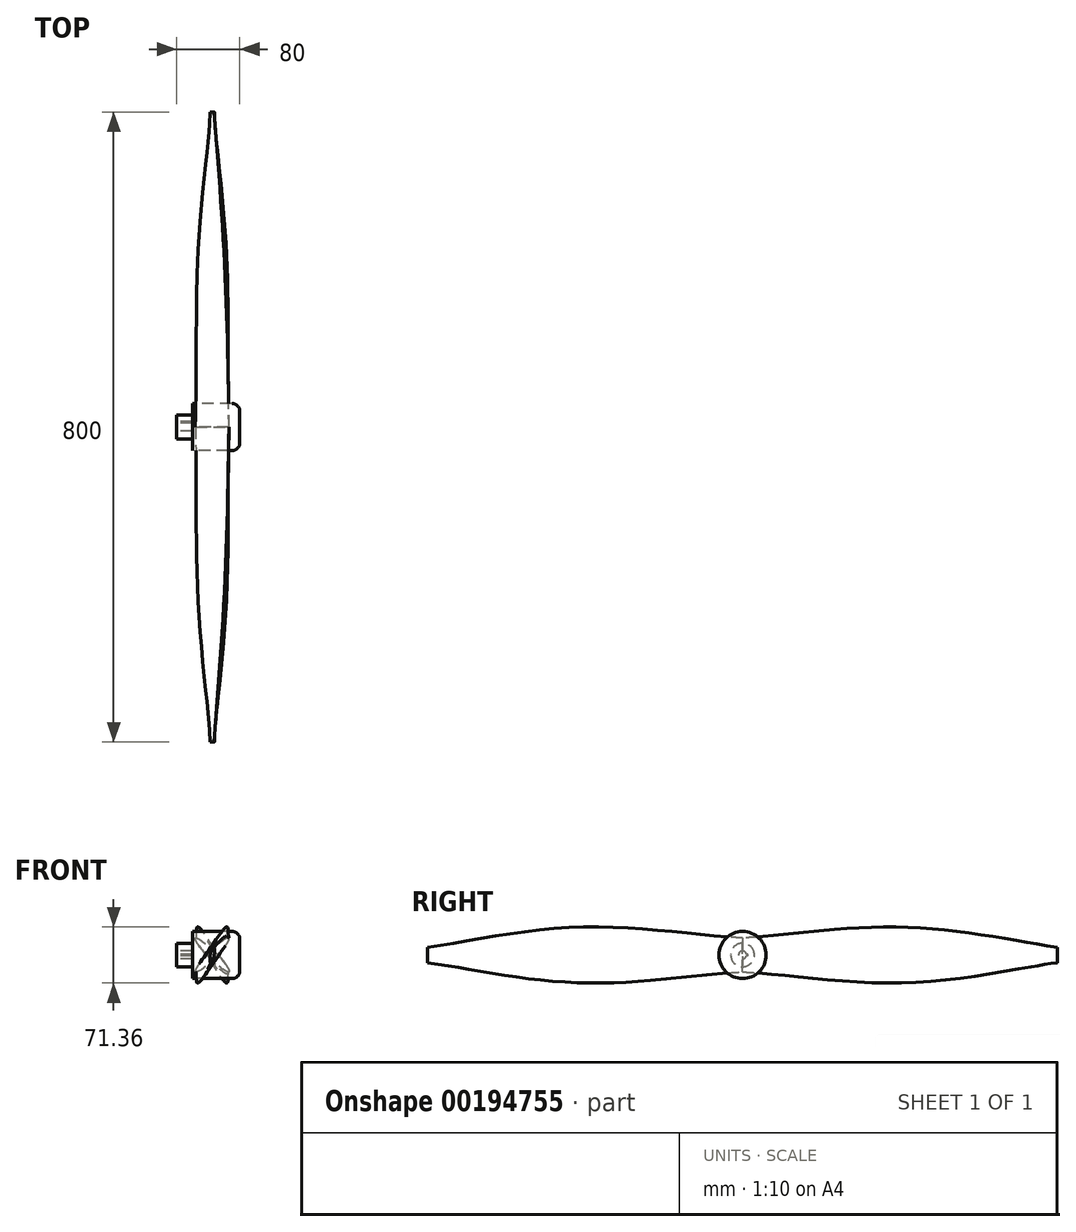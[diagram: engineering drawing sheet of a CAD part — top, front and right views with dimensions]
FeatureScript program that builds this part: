
annotation { "Feature Type Name" : "Feature", "Feature Type Description" : "" }
export const myFeature = defineFeature(function(context is Context, id is Id, definition is map)
    precondition{}
    {
        {
            assignVariable(context, id + "F0", {"name" : "Amplitude", "anyValue" : 400});
        }
        {
            var Q0;
            Q0=qCreatedBy(makeId("Front.planeOp"),FACE);
            var sketch = newSketch(context, id + "F1", { "sketchPlane" : qUnion([Q0])});
            skEllipse(sketch, "E0", {"center": v(0, 0) * mm, "majorRadius": 30 * mm, "minorRadius": 5 * mm, "majorAxis": v(0.7, 0.7)});
            skLineSegment(sketch, "E1", {"start": v(-21.21, -21.21) * mm, "end": v(21.21, 21.21) * mm, "construction": true});
            skLineSegment(sketch, "E2", {"start": v(-3.54, 3.54) * mm, "end": v(3.54, -3.54) * mm, "construction": true});
            skPoint(sketch, "E2.startSnap0", {"position": v(-3.54, 3.54) * mm});
            skSolve(sketch);
        }
        {
            var Q0;
            Q0=qCreatedBy(makeId("Front.planeOp"),FACE);
            cPlane(context, id + "F2", {"entities" : qUnion([Q0]), "cplaneType" : CPlaneType.OFFSET, "offset" : (getVariable(context, 'Amplitude') / 2) * mm, "width" : 150 * mm, "height" : 150 * mm});
        }
        {
            var Q0;
            Q0=qCreatedBy(id+"F2.planeOp",FACE);
            var sketch = newSketch(context, id + "F3", { "sketchPlane" : qUnion([Q0])});
            skEllipse(sketch, "E3", {"center": v(0, 0) * mm, "majorRadius": 40 * mm, "minorRadius": 5 * mm, "majorAxis": v(0.46, 0.89)});
            skLineSegment(sketch, "E4", {"start": v(-18.47, -35.48) * mm, "end": v(18.47, 35.48) * mm, "construction": true});
            skPoint(sketch, "E4.startSnap0", {"position": v(-18.47, -35.48) * mm});
            skLineSegment(sketch, "E5", {"start": v(-4.44, 2.3) * mm, "end": v(4.44, -2.3) * mm, "construction": true});
            skSolve(sketch);
        }
        {
            var Q0;
            Q0=qCreatedBy(makeId("Front.planeOp"),FACE);
            cPlane(context, id + "F4", {"entities" : qUnion([Q0]), "cplaneType" : CPlaneType.OFFSET, "offset" : (getVariable(context, 'Amplitude')) * mm, "width" : 150 * mm, "height" : 150 * mm});
        }
        {
            var Q0;
            Q0=qCreatedBy(id+"F4.planeOp",FACE);
            var sketch = newSketch(context, id + "F5", { "sketchPlane" : qUnion([Q0])});
            skEllipse(sketch, "E6", {"center": v(0, 0) * mm, "majorRadius": 10 * mm, "minorRadius": 2.5 * mm, "majorAxis": v(0.17, 0.98)});
            skLineSegment(sketch, "E7", {"start": v(1.74, 9.85) * mm, "end": v(-1.74, -9.85) * mm, "construction": true});
            skLineSegment(sketch, "E8", {"start": v(-2.46, 0.43) * mm, "end": v(2.46, -0.43) * mm, "construction": true});
            skSolve(sketch);
        }
        {
            var Q0;
            Q0 = qSketchRegion(id + "F1", true);
            var Q1;
            Q1 = qSketchRegion(id + "F3", true);
            var Q2;
            Q2 = qSketchRegion(id + "F5", true);
            loft(context, id + "F6", {"sheetProfilesArray" : [{ "sheetProfileEntities" : qUnion([Q0]) }, { "sheetProfileEntities" : qUnion([Q1]) }, { "sheetProfileEntities" : qUnion([Q2]) }]});
        }
        {
            var Q0;
            Q0=qCreatedBy(makeId("Front.planeOp"),FACE);
            var sketch = newSketch(context, id + "F7", { "sketchPlane" : qUnion([Q0])});
            skLineSegment(sketch, "E9", {"start": v(-194.8, 0) * mm, "end": v(146.61, 0) * mm, "construction": true});
            skSolve(sketch);
        }
        {
            var Q0;
            Q0=makeQuery(id+"F6.opLoft","SWEPT_BODY",BODY,{"disambiguationData":[OSD([makeQuery(id+"F1.imprint","IMPRINT",FACE,{"disambiguationData":[TD([[makeQuery(id+"F1.imprint","IMPRINT",EDGE,{"derivedFrom":sQuery(id+"F1.wireOp",EDGE,"E0")}),1.0]])]}),sQuery(id+"F3.wireOp",EDGE,"E3"),makeQuery(id+"F5.imprint","IMPRINT",FACE,{"disambiguationData":[TD([[makeQuery(id+"F5.imprint","IMPRINT",EDGE,{"derivedFrom":sQuery(id+"F5.wireOp",EDGE,"E6")}),1.0]])]})])]});
            var Q1;
            Q1=sQuery(id+"F7.wireOp",EDGE,"E9");
            circularPattern(context, id + "F8", {"entities" : qUnion([Q0]), "axis" : qUnion([Q1]), "angle" : 360 * degree, "instanceCount" : 2, "equalSpace" : true});
        }
        {
            var Q0;
            Q0=qCreatedBy(makeId("Front.planeOp"),FACE);
            var sketch = newSketch(context, id + "F9", { "sketchPlane" : qUnion([Q0])});
            skLineSegment(sketch, "E10", {"start": v(-45, 0) * mm, "end": v(35, 0) * mm});
            skLineSegment(sketch, "E11", {"start": v(35, 0) * mm, "end": v(35, 30) * mm});
            skLineSegment(sketch, "E12", {"start": v(35, 30) * mm, "end": v(-25, 30) * mm});
            skLineSegment(sketch, "E13", {"start": v(-25, 30) * mm, "end": v(-25, 15) * mm});
            skLineSegment(sketch, "E14", {"start": v(-25, 15) * mm, "end": v(-45, 15) * mm});
            skLineSegment(sketch, "E15", {"start": v(-45, 15) * mm, "end": v(-45, 0) * mm});
            skLineSegment(sketch, "E16", {"start": v(-86.04, 0) * mm, "end": v(72.65, 0) * mm, "construction": true});
            skSolve(sketch);
        }
        {
            var Q0;
            Q0 = qSketchRegion(id + "F9", true);
            var Q1;
            Q1=sQuery(id+"F9.wireOp",EDGE,"E16");
            revolve(context, id + "F10", {"entities" : qUnion([Q0]), "axis" : qUnion([Q1]), "revolveType" : RevolveType.FULL});
        }
        {
            var Q0;
            Q0=makeQuery(id+"F10.opRevolve","SWEPT_EDGE",EDGE,{"disambiguationData":[OSD([sQuery(id+"F9.wireOp",EDGE,"E11"),sQuery(id+"F9.wireOp",EDGE,"E12")])]});
            fillet(context, id + "F11", {"entities" : qUnion([Q0]), "radius" : 10 * mm, "tangentPropagation" : true, "allowEdgeOverflow" : false});
        }
        {
            var Q0;
            Q0=makeQuery(id+"F10.opRevolve","SWEPT_FACE",FACE,{"disambiguationData":[OSD([sQuery(id+"F9.wireOp",EDGE,"E15")])]});
            var sketch = newSketch(context, id + "F12", { "sketchPlane" : qUnion([Q0])});
            skArc(sketch, "E17", {"start": v(-4.9, -1) * mm, "mid": v(5, 0) * mm, "end": v(-4.9, 1) * mm});
            skLineSegment(sketch, "E18.bottom", {"start": v(-6.9, -1) * mm, "end": v(-4.9, -1) * mm});
            skLineSegment(sketch, "E18.top", {"start": v(-6.9, 1) * mm, "end": v(-4.9, 1) * mm});
            skLineSegment(sketch, "E18.left", {"start": v(-6.9, -1) * mm, "end": v(-6.9, 1) * mm});
            skSolve(sketch);
        }
        {
            var Q0;
            Q0 = qSketchRegion(id + "F12", true);
            extrude(context, id + "F13", {"entities" : qUnion([Q0]), "operationType" : NewBodyOperationType.REMOVE, "oppositeDirection" : true, "depth" : 20 * mm});
        }
    });
